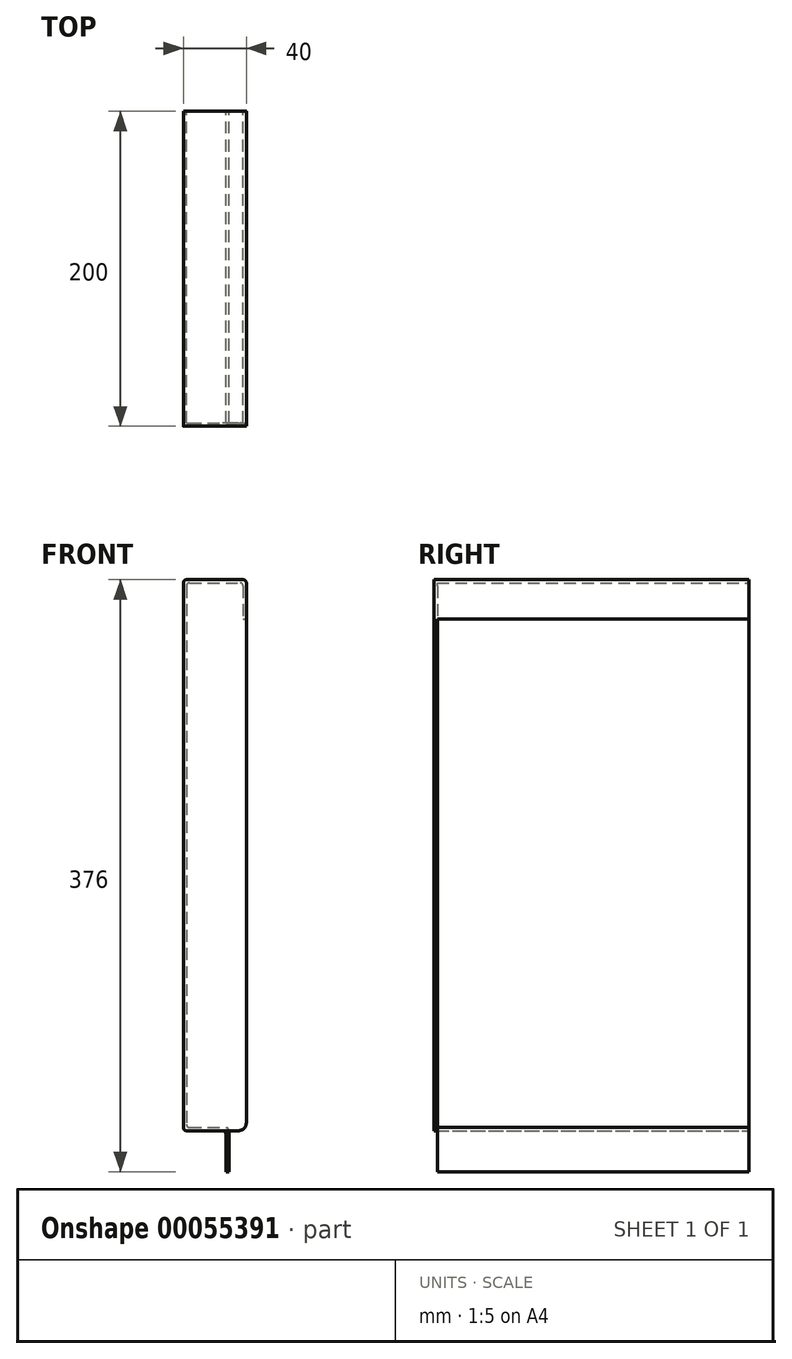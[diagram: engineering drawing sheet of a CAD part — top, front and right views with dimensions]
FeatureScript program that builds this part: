
annotation { "Feature Type Name" : "Feature", "Feature Type Description" : "" }
export const myFeature = defineFeature(function(context is Context, id is Id, definition is map)
    precondition{}
    {
        {
            var Q0;
            Q0=qCreatedBy(makeId("Front.planeOp"),FACE);
            var sketch = newSketch(context, id + "F0", { "sketchPlane" : qUnion([Q0])});
            skLineSegment(sketch, "E0", {"start": v(0, 0) * mm, "end": v(0, -350) * mm});
            skLineSegment(sketch, "E1", {"start": v(0, -350) * mm, "end": v(27, -350) * mm});
            skLineSegment(sketch, "E2", {"start": v(27, -350) * mm, "end": v(27, -376) * mm});
            skLineSegment(sketch, "E3", {"start": v(0, 0) * mm, "end": v(40, 0) * mm});
            skLineSegment(sketch, "E4", {"start": v(40, 0) * mm, "end": v(40, -25) * mm});
            skLineSegment(sketch, "E5.0", {"start": v(38, -2) * mm, "end": v(38, -25) * mm});
            skLineSegment(sketch, "E5.1", {"start": v(29, -348) * mm, "end": v(29, -376) * mm});
            skLineSegment(sketch, "E5.2", {"start": v(2, -348) * mm, "end": v(29, -348) * mm});
            skLineSegment(sketch, "E5.3", {"start": v(2, -2) * mm, "end": v(2, -348) * mm});
            skLineSegment(sketch, "E5.4", {"start": v(2, -2) * mm, "end": v(38, -2) * mm});
            skLineSegment(sketch, "E6", {"start": v(38, -25) * mm, "end": v(40, -25) * mm});
            skLineSegment(sketch, "E7", {"start": v(27, -376) * mm, "end": v(29, -376) * mm});
            skSolve(sketch);
        }
        {
            var Q0;
            Q0=qCreatedBy(makeId("Top.planeOp"),FACE);
            var sketch = newSketch(context, id + "F1", { "sketchPlane" : qUnion([Q0])});
            skLineSegment(sketch, "E8", {"start": v(0, 0) * mm, "end": v(0, 198) * mm});
            skSolve(sketch);
        }
        {
            var Q0;
            Q0=qSketchRegion(id+"F0",true);
            var Q1;
            Q1=qConstructionFilter(qBodyType(qCreatedBy(id+"F1",EDGE),BodyType.WIRE),ConstructionObject.NO);
            sweep(context, id + "F2", {"profiles" : qUnion([Q0]), "path" : qUnion([Q1])});
        }
        {
            var Q0;
            Q0=makeQuery(id+"F2.opSweep","CAP_FACE",FACE,{"disambiguationData":[OSD([sQuery(id+"F0.wireOp",EDGE,"E0"),sQuery(id+"F0.wireOp",EDGE,"E1"),sQuery(id+"F0.wireOp",EDGE,"E2"),sQuery(id+"F0.wireOp",EDGE,"E3"),sQuery(id+"F0.wireOp",EDGE,"E4"),sQuery(id+"F0.wireOp",EDGE,"E5.0"),sQuery(id+"F0.wireOp",EDGE,"E5.1"),sQuery(id+"F0.wireOp",EDGE,"E5.2"),sQuery(id+"F0.wireOp",EDGE,"E5.3"),sQuery(id+"F0.wireOp",EDGE,"E5.4"),sQuery(id+"F0.wireOp",EDGE,"E6"),sQuery(id+"F0.wireOp",EDGE,"E7"),sQuery(id+"F1.wireOp",VERTEX,"E8.start")])],"isStart":true});
            var sketch = newSketch(context, id + "F3", { "sketchPlane" : qUnion([Q0])});
            skLineSegment(sketch, "E9.0", {"start": v(40, 0) * mm, "end": v(0, 0) * mm});
            skLineSegment(sketch, "E10.0", {"start": v(0, -350) * mm, "end": v(0, 0) * mm});
            skPoint(sketch, "E11.0.end.orphan", {"position": v(27, -350) * mm});
            skPoint(sketch, "E12.0.start.orphan", {"position": v(40, -25) * mm});
            skLineSegment(sketch, "E13", {"start": v(40, 0) * mm, "end": v(40, -345) * mm});
            skLineSegment(sketch, "E14", {"start": v(35, -350) * mm, "end": v(0, -350) * mm});
            skPoint(sketch, "E15.visualSharp", {"position": v(40, -350) * mm});
            skArc(sketch, "E15.filletArc", {"start": v(35, -350) * mm, "mid": v(38.54, -348.54) * mm, "end": v(40, -345) * mm});
            skSolve(sketch);
        }
        {
            var Q0;
            Q0=qSketchRegion(id+"F3",true);
            extrude(context, id + "F4", {"entities" : qUnion([Q0]), "depth" : 2 * mm});
        }
        {
            var Q0;
            Q0=makeQuery(id+"F2.opSweep","SWEPT_BODY",BODY,{"disambiguationData":[OSD([sQuery(id+"F0.wireOp",EDGE,"E0"),sQuery(id+"F0.wireOp",EDGE,"E1"),sQuery(id+"F0.wireOp",EDGE,"E2"),sQuery(id+"F0.wireOp",EDGE,"E3"),sQuery(id+"F0.wireOp",EDGE,"E4"),sQuery(id+"F0.wireOp",EDGE,"E5.0"),sQuery(id+"F0.wireOp",EDGE,"E5.1"),sQuery(id+"F0.wireOp",EDGE,"E5.2"),sQuery(id+"F0.wireOp",EDGE,"E5.3"),sQuery(id+"F0.wireOp",EDGE,"E5.4"),sQuery(id+"F0.wireOp",EDGE,"E6"),sQuery(id+"F0.wireOp",EDGE,"E7"),sQuery(id+"F1.wireOp",EDGE,"E8")])]});
            var Q1;
            Q1=makeQuery(id+"F4.opExtrude","SWEPT_BODY",BODY,{"disambiguationData":[OSD([sQuery(id+"F3.wireOp",EDGE,"E9.0"),sQuery(id+"F3.wireOp",EDGE,"E10.0"),sQuery(id+"F3.wireOp",EDGE,"E13"),sQuery(id+"F3.wireOp",EDGE,"E14"),sQuery(id+"F3.wireOp",EDGE,"E15.filletArc")])]});
            booleanBodies(context, id + "F5", {"operationType" : BooleanOperationType.UNION, "tools" : qUnion([Q0, Q1])});
        }
        {
            var Q0;
            Q0=makeQuery(id+"F5.opBoolean","MERGE",EDGE,{"derivedFrom":[makeQuery(id+"F2.opSweep","SWEPT_EDGE",EDGE,{"disambiguationData":[OSD([sQuery(id+"F0.wireOp",EDGE,"E3"),sQuery(id+"F0.wireOp",EDGE,"E4"),sQuery(id+"F1.wireOp",EDGE,"E8")])]}),makeQuery(id+"F4.opExtrude","SWEPT_EDGE",EDGE,{"disambiguationData":[OSD([sQuery(id+"F3.wireOp",EDGE,"E9.0"),sQuery(id+"F3.wireOp",EDGE,"E13")])]})]});
            var Q1;
            Q1=makeQuery(id+"F5.opBoolean","MERGE",EDGE,{"derivedFrom":[makeQuery(id+"F2.opSweep","SWEPT_EDGE",EDGE,{"disambiguationData":[OSD([sQuery(id+"F0.wireOp",EDGE,"E0"),sQuery(id+"F0.wireOp",EDGE,"E3"),sQuery(id+"F1.wireOp",EDGE,"E8")])]}),makeQuery(id+"F4.opExtrude","SWEPT_EDGE",EDGE,{"disambiguationData":[OSD([sQuery(id+"F3.wireOp",EDGE,"E9.0"),sQuery(id+"F3.wireOp",EDGE,"E10.0")])]})]});
            var Q2;
            Q2=makeQuery(id+"F2.opSweep","SWEPT_EDGE",EDGE,{"disambiguationData":[OSD([sQuery(id+"F0.wireOp",EDGE,"E5.2"),sQuery(id+"F0.wireOp",EDGE,"E5.3"),sQuery(id+"F1.wireOp",EDGE,"E8")])]});
            var Q3;
            Q3=makeQuery(id+"F2.opSweep","SWEPT_EDGE",EDGE,{"disambiguationData":[OSD([sQuery(id+"F0.wireOp",EDGE,"E5.1"),sQuery(id+"F0.wireOp",EDGE,"E5.2"),sQuery(id+"F1.wireOp",EDGE,"E8")])]});
            var Q4;
            Q4=makeQuery(id+"F2.opSweep","SWEPT_EDGE",EDGE,{"disambiguationData":[OSD([sQuery(id+"F0.wireOp",EDGE,"E1"),sQuery(id+"F0.wireOp",EDGE,"E2"),sQuery(id+"F1.wireOp",EDGE,"E8")])]});
            var Q5;
            Q5=makeQuery(id+"F5.opBoolean","MERGE",EDGE,{"derivedFrom":[makeQuery(id+"F2.opSweep","SWEPT_EDGE",EDGE,{"disambiguationData":[OSD([sQuery(id+"F0.wireOp",EDGE,"E0"),sQuery(id+"F0.wireOp",EDGE,"E1"),sQuery(id+"F1.wireOp",EDGE,"E8")])]}),makeQuery(id+"F4.opExtrude","SWEPT_EDGE",EDGE,{"disambiguationData":[OSD([sQuery(id+"F3.wireOp",EDGE,"E10.0"),sQuery(id+"F3.wireOp",EDGE,"E14")])]})]});
            var Q6;
            Q6=makeQuery(id+"F2.opSweep","SWEPT_EDGE",EDGE,{"disambiguationData":[OSD([sQuery(id+"F0.wireOp",EDGE,"E5.3"),sQuery(id+"F0.wireOp",EDGE,"E5.4"),sQuery(id+"F1.wireOp",EDGE,"E8")])]});
            var Q7;
            Q7=makeQuery(id+"F2.opSweep","SWEPT_EDGE",EDGE,{"disambiguationData":[OSD([sQuery(id+"F0.wireOp",EDGE,"E5.0"),sQuery(id+"F0.wireOp",EDGE,"E5.4"),sQuery(id+"F1.wireOp",EDGE,"E8")])]});
            fillet(context, id + "F6", {"entities" : qUnion([Q0, Q1, Q2, Q3, Q4, Q5, Q6, Q7]), "radius" : 2 * mm, "tangentPropagation" : true, "allowEdgeOverflow" : false});
        }
    });
